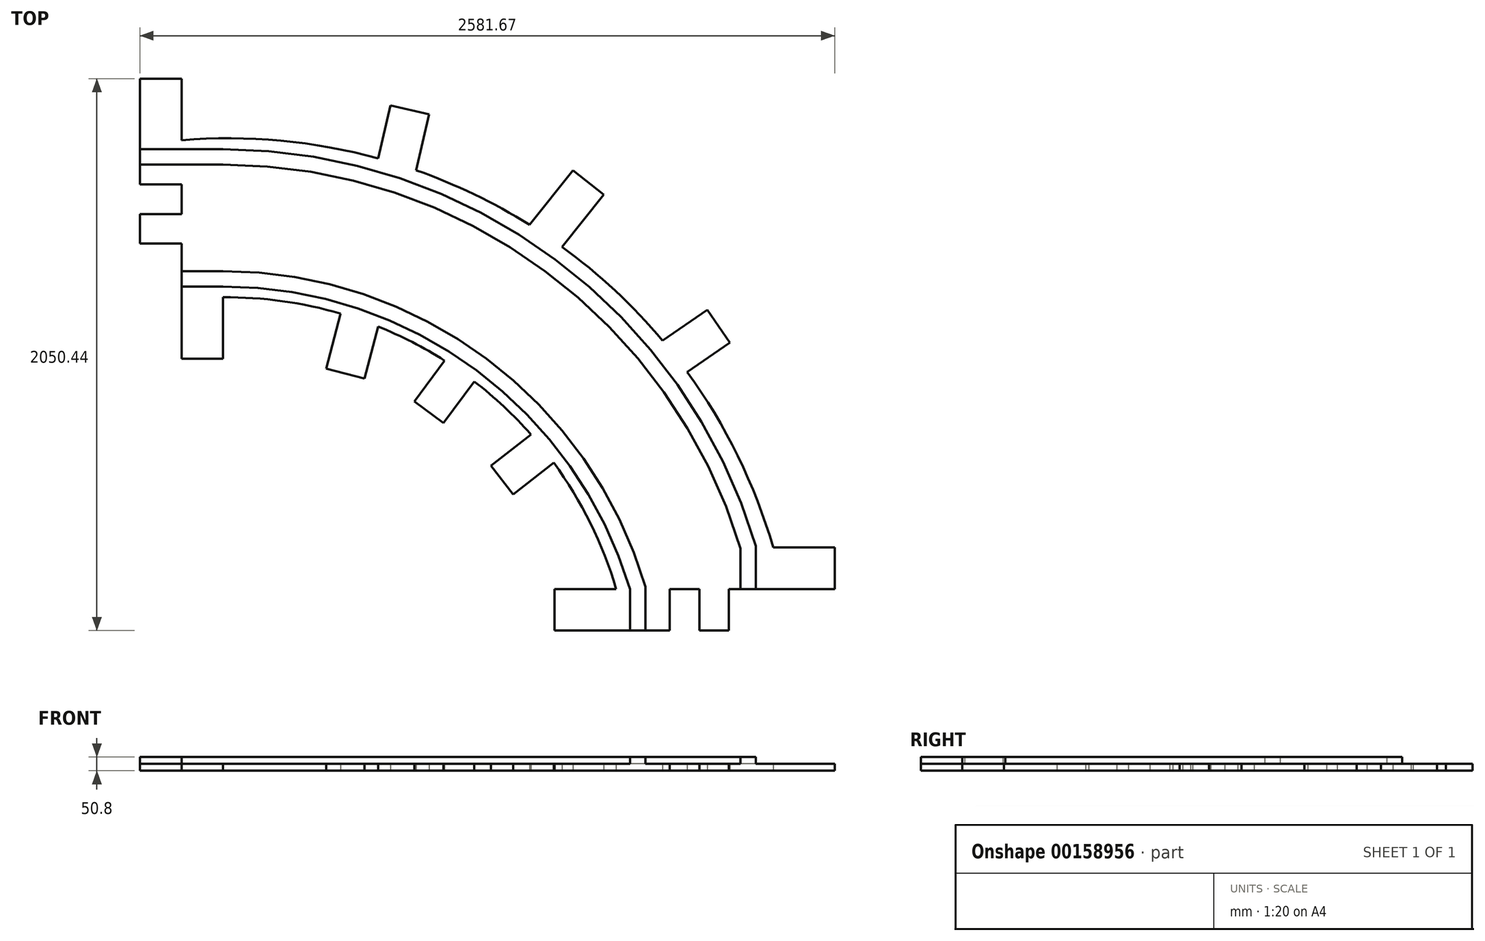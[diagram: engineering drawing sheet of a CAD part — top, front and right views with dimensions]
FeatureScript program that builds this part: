
annotation { "Feature Type Name" : "Feature", "Feature Type Description" : "" }
export const myFeature = defineFeature(function(context is Context, id is Id, definition is map)
    precondition{}
    {
        {
            var Q0;
            Q0=qCreatedBy(makeId("Top.planeOp"),FACE);
            var sketch = newSketch(context, id + "F0", { "sketchPlane" : qUnion([Q0])});
            skLineSegment(sketch, "E0", {"start": v(-123.12, 340.2) * mm, "end": v(-123.12, -52.81) * mm});
            skLineSegment(sketch, "E1", {"start": v(-123.12, -52.81) * mm, "end": v(31.19, -52.81) * mm});
            skLineSegment(sketch, "E2", {"start": v(31.19, -52.81) * mm, "end": v(31.19, -162.82) * mm});
            skLineSegment(sketch, "E3", {"start": v(31.19, -162.82) * mm, "end": v(-123.12, -162.82) * mm});
            skLineSegment(sketch, "E4", {"start": v(-123.12, -162.82) * mm, "end": v(-123.12, -272.82) * mm});
            skLineSegment(sketch, "E5", {"start": v(-123.12, -272.82) * mm, "end": v(31.19, -272.82) * mm});
            skLineSegment(sketch, "E6", {"start": v(31.19, -272.82) * mm, "end": v(31.19, -700.69) * mm});
            skLineSegment(sketch, "E7", {"start": v(2458.55, -1555.94) * mm, "end": v(2065.54, -1555.94) * mm});
            skLineSegment(sketch, "E8", {"start": v(2065.54, -1555.94) * mm, "end": v(2065.54, -1710.24) * mm});
            skLineSegment(sketch, "E9", {"start": v(2065.54, -1710.24) * mm, "end": v(1955.53, -1710.24) * mm});
            skLineSegment(sketch, "E10", {"start": v(1955.53, -1710.24) * mm, "end": v(1955.53, -1555.94) * mm});
            skLineSegment(sketch, "E11", {"start": v(1955.53, -1555.94) * mm, "end": v(1845.52, -1555.94) * mm});
            skLineSegment(sketch, "E12", {"start": v(1845.52, -1555.94) * mm, "end": v(1845.52, -1710.24) * mm});
            skLineSegment(sketch, "E13", {"start": v(1845.52, -1710.24) * mm, "end": v(1417.66, -1710.24) * mm});
            skLineSegment(sketch, "E14", {"start": v(-123.12, 340.2) * mm, "end": v(31.19, 340.2) * mm});
            skLineSegment(sketch, "E15", {"start": v(31.19, 340.2) * mm, "end": v(31.19, 111.7) * mm});
            skLineSegment(sketch, "E16", {"start": v(2458.55, -1555.94) * mm, "end": v(2458.55, -1401.63) * mm});
            skLineSegment(sketch, "E17", {"start": v(2458.55, -1401.63) * mm, "end": v(2230.06, -1401.63) * mm});
            skLineSegment(sketch, "E18", {"start": v(31.19, -700.69) * mm, "end": v(185.5, -700.69) * mm});
            skLineSegment(sketch, "E19", {"start": v(185.5, -700.69) * mm, "end": v(185.5, -472.19) * mm});
            skLineSegment(sketch, "E20", {"start": v(1417.66, -1710.24) * mm, "end": v(1417.66, -1555.94) * mm});
            skLineSegment(sketch, "E21", {"start": v(1417.66, -1555.94) * mm, "end": v(1646.16, -1555.94) * mm});
            skArc(sketch, "E22", {"start": v(2230.06, -1401.63) * mm, "mid": v(1400.55, -252.77) * mm, "end": v(31.19, 111.7) * mm});
            skArc(sketch, "E23", {"start": v(1646.16, -1555.94) * mm, "mid": v(1097.84, -768.75) * mm, "end": v(185.5, -472.19) * mm});
            skLineSegment(sketch, "E24", {"start": v(622.9, -532.64) * mm, "end": v(569.25, -736.82) * mm});
            skLineSegment(sketch, "E25", {"start": v(569.25, -736.82) * mm, "end": v(711.49, -774.2) * mm});
            skLineSegment(sketch, "E26", {"start": v(711.49, -774.2) * mm, "end": v(762.28, -580.9) * mm});
            skLineSegment(sketch, "E27", {"start": v(1008.82, -707.53) * mm, "end": v(896.3, -858.64) * mm});
            skLineSegment(sketch, "E28", {"start": v(896.3, -858.64) * mm, "end": v(1004.64, -939.3) * mm});
            skLineSegment(sketch, "E29", {"start": v(1004.64, -939.3) * mm, "end": v(1119.46, -785.1) * mm});
            skLineSegment(sketch, "E30", {"start": v(1329.87, -981.94) * mm, "end": v(1180.76, -1097.54) * mm});
            skLineSegment(sketch, "E31", {"start": v(1180.76, -1097.54) * mm, "end": v(1263.3, -1204) * mm});
            skLineSegment(sketch, "E32", {"start": v(1263.3, -1204) * mm, "end": v(1414.4, -1086.87) * mm});
            skLineSegment(sketch, "E33", {"start": v(762.28, 43.92) * mm, "end": v(807.94, 241.05) * mm});
            skLineSegment(sketch, "E34", {"start": v(807.94, 241.05) * mm, "end": v(951.13, 207.94) * mm});
            skLineSegment(sketch, "E35", {"start": v(951.13, 207.94) * mm, "end": v(903.05, 0) * mm});
            skLineSegment(sketch, "E36", {"start": v(1324.29, -202.68) * mm, "end": v(1485.87, 0) * mm});
            skLineSegment(sketch, "E37", {"start": v(1485.87, 0) * mm, "end": v(1599.81, -90.84) * mm});
            skLineSegment(sketch, "E38", {"start": v(1599.81, -90.84) * mm, "end": v(1445.4, -284.5) * mm});
            skLineSegment(sketch, "E39", {"start": v(1819.14, -632.88) * mm, "end": v(1985.43, -518.5) * mm});
            skLineSegment(sketch, "E40", {"start": v(1985.43, -518.5) * mm, "end": v(2068.94, -639.9) * mm});
            skLineSegment(sketch, "E41", {"start": v(2068.94, -639.9) * mm, "end": v(1910.13, -749.14) * mm});
            skSolve(sketch);
        }
        {
            var Q0;
            Q0=qSketchRegion(id+"F0",true);
            extrude(context, id + "F1", {"entities" : qUnion([Q0]), "depth" : 25.4 * mm});
        }
        {
            var Q0;
            Q0=makeQuery(id+"F1.opExtrude","CAP_FACE",FACE,{"disambiguationData":[OSD([sQuery(id+"F0.wireOp",EDGE,"E0"),sQuery(id+"F0.wireOp",EDGE,"E1"),sQuery(id+"F0.wireOp",EDGE,"E2"),sQuery(id+"F0.wireOp",EDGE,"E3"),sQuery(id+"F0.wireOp",EDGE,"E4"),sQuery(id+"F0.wireOp",EDGE,"E5"),sQuery(id+"F0.wireOp",EDGE,"E6"),sQuery(id+"F0.wireOp",EDGE,"E7"),sQuery(id+"F0.wireOp",EDGE,"E8"),sQuery(id+"F0.wireOp",EDGE,"E9"),sQuery(id+"F0.wireOp",EDGE,"E10"),sQuery(id+"F0.wireOp",EDGE,"E11"),sQuery(id+"F0.wireOp",EDGE,"E12"),sQuery(id+"F0.wireOp",EDGE,"E13"),sQuery(id+"F0.wireOp",EDGE,"E14"),sQuery(id+"F0.wireOp",EDGE,"E15"),sQuery(id+"F0.wireOp",EDGE,"E16"),sQuery(id+"F0.wireOp",EDGE,"E17"),sQuery(id+"F0.wireOp",EDGE,"E18"),sQuery(id+"F0.wireOp",EDGE,"E19"),sQuery(id+"F0.wireOp",EDGE,"E20"),sQuery(id+"F0.wireOp",EDGE,"E21"),sQuery(id+"F0.wireOp",EDGE,"E22"),sQuery(id+"F0.wireOp",EDGE,"E23"),sQuery(id+"F0.wireOp",EDGE,"E24"),sQuery(id+"F0.wireOp",EDGE,"E25"),sQuery(id+"F0.wireOp",EDGE,"E26"),sQuery(id+"F0.wireOp",EDGE,"E27"),sQuery(id+"F0.wireOp",EDGE,"E28"),sQuery(id+"F0.wireOp",EDGE,"E29"),sQuery(id+"F0.wireOp",EDGE,"E30"),sQuery(id+"F0.wireOp",EDGE,"E31"),sQuery(id+"F0.wireOp",EDGE,"E32"),sQuery(id+"F0.wireOp",EDGE,"E33"),sQuery(id+"F0.wireOp",EDGE,"E34"),sQuery(id+"F0.wireOp",EDGE,"E35"),sQuery(id+"F0.wireOp",EDGE,"E36"),sQuery(id+"F0.wireOp",EDGE,"E37"),sQuery(id+"F0.wireOp",EDGE,"E38"),sQuery(id+"F0.wireOp",EDGE,"E39"),sQuery(id+"F0.wireOp",EDGE,"E40"),sQuery(id+"F0.wireOp",EDGE,"E41")])],"isStart":false});
            var sketch = newSketch(context, id + "F2", { "sketchPlane" : qUnion([Q0])});
            skLineSegment(sketch, "E42", {"start": v(31.19, -432.08) * mm, "end": v(185.43, -432.08) * mm});
            skLineSegment(sketch, "E43", {"start": v(-123.12, 77.71) * mm, "end": v(185.43, 77.71) * mm});
            skLineSegment(sketch, "E44", {"start": v(2165.73, -1555.94) * mm, "end": v(2165.73, -1396.56) * mm});
            skLineSegment(sketch, "E45", {"start": v(1697.89, -1710.24) * mm, "end": v(1697.89, -1555.94) * mm});
            skArc(sketch, "E46", {"start": v(1697.89, -1555.94) * mm, "mid": v(1127.58, -743.8) * mm, "end": v(185.43, -432.08) * mm});
            skArc(sketch, "E47", {"start": v(2165.73, -1396.56) * mm, "mid": v(1419.83, -331.32) * mm, "end": v(185.43, 77.71) * mm});
            skLineSegment(sketch, "E48.0", {"start": v(-123.12, 20.56) * mm, "end": v(185.43, 20.56) * mm});
            skArc(sketch, "E48.1", {"start": v(2108.58, -1404.99) * mm, "mid": v(1382.37, -374.69) * mm, "end": v(185.43, 20.56) * mm});
            skLineSegment(sketch, "E48.2", {"start": v(2108.58, -1555.94) * mm, "end": v(2108.58, -1404.99) * mm});
            skLineSegment(sketch, "E49.0", {"start": v(31.19, -374.93) * mm, "end": v(185.43, -374.93) * mm});
            skArc(sketch, "E49.1", {"start": v(1755.04, -1547.6) * mm, "mid": v(1165.07, -700.47) * mm, "end": v(185.43, -374.93) * mm});
            skLineSegment(sketch, "E49.2", {"start": v(1755.04, -1710.24) * mm, "end": v(1755.04, -1547.6) * mm});
            skLineSegment(sketch, "E50", {"start": v(31.19, -374.93) * mm, "end": v(31.19, -432.08) * mm});
            skLineSegment(sketch, "E51", {"start": v(-123.12, 77.71) * mm, "end": v(-123.12, 20.56) * mm});
            skLineSegment(sketch, "E52", {"start": v(1697.89, -1710.24) * mm, "end": v(1755.04, -1710.24) * mm});
            skLineSegment(sketch, "E53", {"start": v(2108.58, -1555.94) * mm, "end": v(2165.73, -1555.94) * mm});
            skSolve(sketch);
        }
        {
            var Q0;
            Q0=qSketchRegion(id+"F2",true);
            extrude(context, id + "F3", {"entities" : qUnion([Q0]), "operationType" : NewBodyOperationType.ADD, "depth" : 25.4 * mm});
        }
    });
